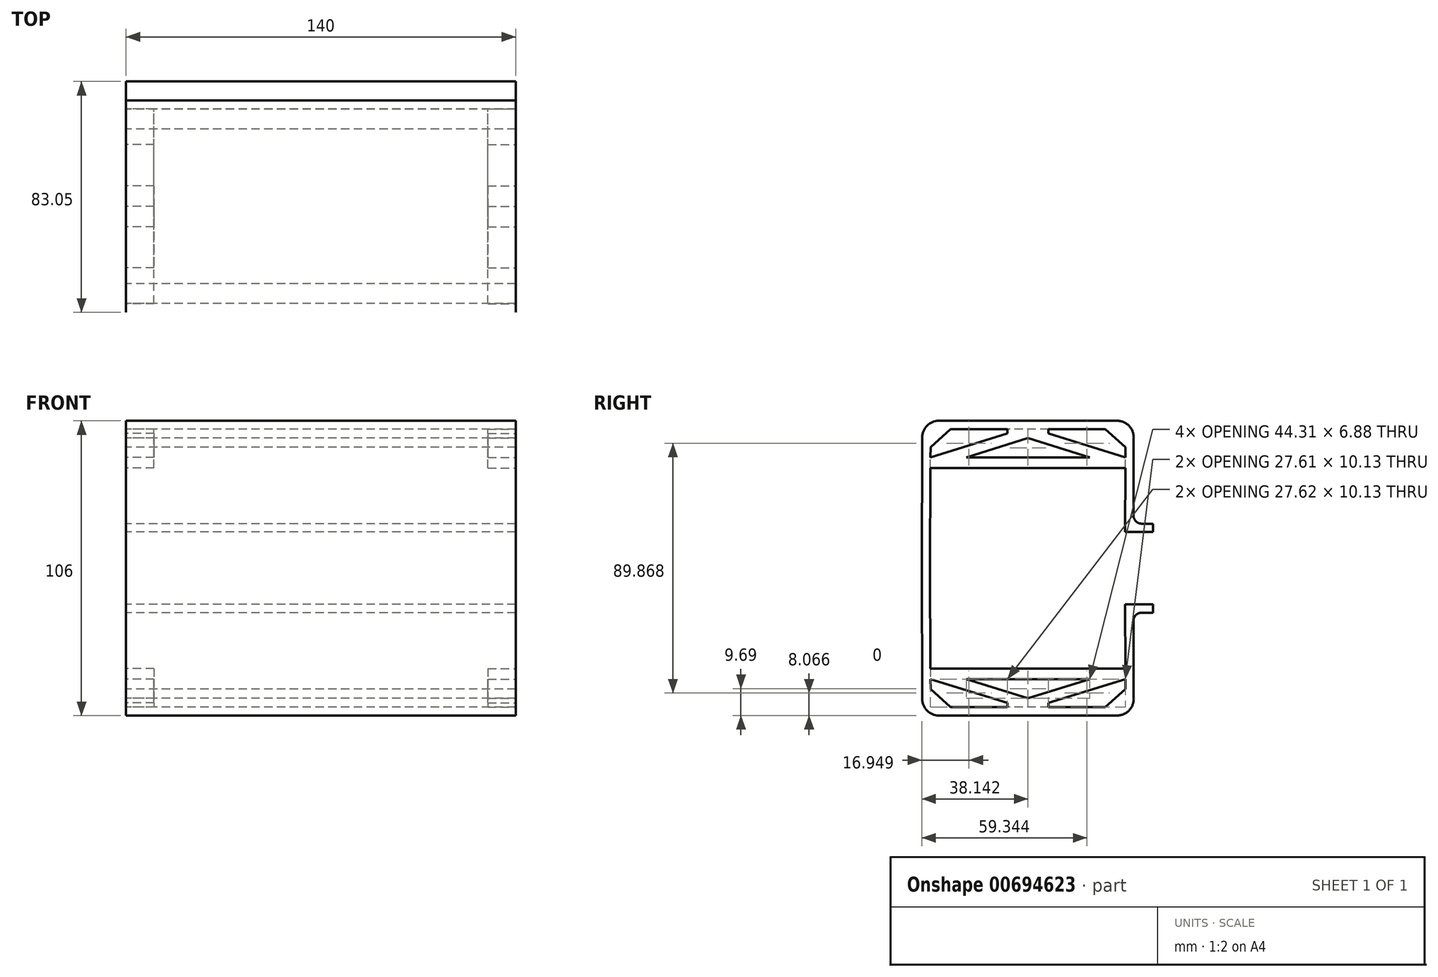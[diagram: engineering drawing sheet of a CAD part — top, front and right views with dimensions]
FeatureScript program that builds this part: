
annotation { "Feature Type Name" : "Feature", "Feature Type Description" : "" }
export const myFeature = defineFeature(function(context is Context, id is Id, definition is map)
    precondition{}
    {
        {
            var Q0;
            Q0=qCreatedBy(makeId("Right.planeOp"),FACE);
            var sketch = newSketch(context, id + "F0", { "sketchPlane" : qUnion([Q0])});
            skLineSegment(sketch, "E0.top", {"start": v(27.8, -50) * mm, "end": v(-27.8, -50) * mm});
            skLineSegment(sketch, "E0.right", {"start": v(-35.15, 0) * mm, "end": v(-35, -43.47) * mm});
            skPoint(sketch, "E0.middle", {"position": v(0, 0) * mm});
            skPoint(sketch, "E1", {"position": v(34.9, -13) * mm});
            skLineSegment(sketch, "E2.trimOffspring", {"start": v(34.9, -13) * mm, "end": v(35, -43.47) * mm});
            skPoint(sketch, "E3.visualSharp", {"position": v(-34.98, -50) * mm});
            skPoint(sketch, "E4.visualSharp", {"position": v(35.02, -50) * mm});
            skLineSegment(sketch, "E5", {"start": v(34.9, -13) * mm, "end": v(44.9, -13) * mm});
            skLineSegment(sketch, "E6.0", {"start": v(40.92, -16) * mm, "end": v(44.9, -16) * mm});
            skLineSegment(sketch, "E6.6", {"start": v(-38.15, 0) * mm, "end": v(-37.99, -47.01) * mm});
            skArc(sketch, "E6.7", {"start": v(-37.99, -47.01) * mm, "mid": v(-36.23, -51.24) * mm, "end": v(-32, -53) * mm});
            skLineSegment(sketch, "E6.8", {"start": v(32, -53) * mm, "end": v(-32, -53) * mm});
            skArc(sketch, "E6.9", {"start": v(32, -53) * mm, "mid": v(36.34, -51.16) * mm, "end": v(38.01, -46.75) * mm});
            skLineSegment(sketch, "E6.10", {"start": v(37.92, -19.01) * mm, "end": v(38.01, -46.75) * mm});
            skLineSegment(sketch, "E7", {"start": v(44.9, -13) * mm, "end": v(44.9, -16) * mm});
            skPoint(sketch, "E8.visualSharp", {"position": v(37.9, -16) * mm});
            skArc(sketch, "E8.filletArc", {"start": v(40.92, -16) * mm, "mid": v(38.8, -16.88) * mm, "end": v(37.92, -19.01) * mm});
            skLineSegment(sketch, "E9", {"start": v(-35.15, 0) * mm, "end": v(-38.15, 0) * mm});
            skLineSegment(sketch, "E10", {"start": v(-38.15, 0) * mm, "end": v(43.63, 0) * mm, "construction": true});
            skLineSegment(sketch, "E11", {"start": v(-35, -43.47) * mm, "end": v(-27.8, -50) * mm});
            skLineSegment(sketch, "E12", {"start": v(35, -43.47) * mm, "end": v(27.8, -50) * mm});
            skSolve(sketch);
        }
        {
            var Q0;
            Q0=qSketchRegion(id+"F0",true);
            extrude(context, id + "F1", {"entities" : qUnion([Q0]), "depth" : 70 * mm, "offsetDistance" : 25 * mm});
        }
        {
            var Q0;
            Q0=makeQuery(id+"F1.opExtrude","CAP_FACE",FACE,{"disambiguationData":[OSD([sQuery(id+"F0.wireOp",EDGE,"E0.bottom"),sQuery(id+"F0.wireOp",EDGE,"E0.top"),sQuery(id+"F0.wireOp",EDGE,"E0.left"),sQuery(id+"F0.wireOp",EDGE,"E0.right"),sQuery(id+"F0.wireOp",EDGE,"E2.trimOffspring"),sQuery(id+"F0.wireOp",EDGE,"16ec7434-7e19-4c96-ad34-d09fe3e63414.filletArc"),sQuery(id+"F0.wireOp",EDGE,"782e88cc-4596-4778-937f-94acf3693ae4.filletArc"),sQuery(id+"F0.wireOp",EDGE,"E3.filletArc"),sQuery(id+"F0.wireOp",EDGE,"E4.filletArc"),sQuery(id+"F0.wireOp",EDGE,"0f476a3a-29cd-4e09-8ddb-883452e4d05f"),sQuery(id+"F0.wireOp",EDGE,"E5"),sQuery(id+"F0.wireOp",EDGE,"E6.0"),sQuery(id+"F0.wireOp",EDGE,"E6.1"),sQuery(id+"F0.wireOp",EDGE,"E6.2"),sQuery(id+"F0.wireOp",EDGE,"E6.3"),sQuery(id+"F0.wireOp",EDGE,"E6.4"),sQuery(id+"F0.wireOp",EDGE,"E6.5"),sQuery(id+"F0.wireOp",EDGE,"E6.6"),sQuery(id+"F0.wireOp",EDGE,"E6.7"),sQuery(id+"F0.wireOp",EDGE,"E6.8"),sQuery(id+"F0.wireOp",EDGE,"E6.9"),sQuery(id+"F0.wireOp",EDGE,"E6.10"),sQuery(id+"F0.wireOp",EDGE,"E7"),sQuery(id+"F0.wireOp",EDGE,"56edb3b3-d3ca-4cde-a283-c5cd5add8c42"),sQuery(id+"F0.wireOp",EDGE,"E8.filletArc"),sQuery(id+"F0.wireOp",EDGE,"69a5be2d-b862-4d8c-9c8a-7a6ed0181d43.filletArc")])],"isStart":false});
            var sketch = newSketch(context, id + "F2", { "sketchPlane" : qUnion([Q0])});
            skLineSegment(sketch, "E13", {"start": v(-35.03, -36.06) * mm, "end": v(34.98, -36.06) * mm});
            skLineSegment(sketch, "E14", {"start": v(-22.17, -39.87) * mm, "end": v(22.15, -39.87) * mm});
            skLineSegment(sketch, "E15", {"start": v(-35.01, -39.87) * mm, "end": v(-7.39, -48.45) * mm});
            skLineSegment(sketch, "E16", {"start": v(-2.39, -50) * mm, "end": v(2.39, -50) * mm});
            skLineSegment(sketch, "E17", {"start": v(7.39, -48.45) * mm, "end": v(34.99, -39.87) * mm});
            skLineSegment(sketch, "E18", {"start": v(0, -46.75) * mm, "end": v(22.15, -39.87) * mm});
            skLineSegment(sketch, "E19", {"start": v(0, -46.75) * mm, "end": v(-22.17, -39.87) * mm});
            skLineSegment(sketch, "E20", {"start": v(-22.17, -39.87) * mm, "end": v(-23.3, -43.5) * mm, "construction": true});
            skLineSegment(sketch, "E21", {"start": v(22.15, -39.87) * mm, "end": v(23.28, -43.5) * mm, "construction": true});
            skLineSegment(sketch, "E22", {"start": v(-0.03, -36.06) * mm, "end": v(0, -39.87) * mm, "construction": true});
            skLineSegment(sketch, "E23", {"start": v(7.39, -48.45) * mm, "end": v(7.39, -50) * mm});
            skLineSegment(sketch, "E24", {"start": v(-7.39, -48.45) * mm, "end": v(-7.39, -50) * mm});
            skSolve(sketch);
        }
        {
            var Q0;
            {var subQ1=sQuery(id+"F2.wireOp",EDGE,"E13");Q0=makeQuery(id+"F2.imprint","IMPRINT",FACE,{"disambiguationData":[TD([[makeQuery(id+"F2.imprint","IMPRINT",EDGE,{"derivedFrom":subQ1}),-1.0]])]});}
            var Q1;
            {var subQ0=sQuery(id+"F2.wireOp",EDGE,"69ec383f-f7ca-4513-a4e7-9af87f1944310.MirrorCS");Q1=makeQuery(id+"F2.imprint","IMPRINT",FACE,{"disambiguationData":[TD([[makeQuery(id+"F2.imprint","IMPRINT",EDGE,{"derivedFrom":subQ0}),-1.0]])]});}
            extrude(context, id + "F3", {"entities" : qUnion([Q0, Q1]), "operationType" : NewBodyOperationType.ADD, "oppositeDirection" : true, "depth" : 10 * mm, "offsetDistance" : 25 * mm});
        }
        {
            var Q0;
            Q0=makeQuery(id+"F1.opExtrude","SWEPT_BODY",BODY,{"disambiguationData":[OSD([sQuery(id+"F0.wireOp",EDGE,"E0.bottom"),sQuery(id+"F0.wireOp",EDGE,"E0.top"),sQuery(id+"F0.wireOp",EDGE,"E0.left"),sQuery(id+"F0.wireOp",EDGE,"E0.right"),sQuery(id+"F0.wireOp",EDGE,"E2.trimOffspring"),sQuery(id+"F0.wireOp",EDGE,"16ec7434-7e19-4c96-ad34-d09fe3e63414.filletArc"),sQuery(id+"F0.wireOp",EDGE,"782e88cc-4596-4778-937f-94acf3693ae4.filletArc"),sQuery(id+"F0.wireOp",EDGE,"E3.filletArc"),sQuery(id+"F0.wireOp",EDGE,"E4.filletArc"),sQuery(id+"F0.wireOp",EDGE,"0f476a3a-29cd-4e09-8ddb-883452e4d05f"),sQuery(id+"F0.wireOp",EDGE,"E5"),sQuery(id+"F0.wireOp",EDGE,"E6.0"),sQuery(id+"F0.wireOp",EDGE,"E6.1"),sQuery(id+"F0.wireOp",EDGE,"E6.2"),sQuery(id+"F0.wireOp",EDGE,"E6.3"),sQuery(id+"F0.wireOp",EDGE,"E6.4"),sQuery(id+"F0.wireOp",EDGE,"E6.5"),sQuery(id+"F0.wireOp",EDGE,"E6.6"),sQuery(id+"F0.wireOp",EDGE,"E6.7"),sQuery(id+"F0.wireOp",EDGE,"E6.8"),sQuery(id+"F0.wireOp",EDGE,"E6.9"),sQuery(id+"F0.wireOp",EDGE,"E6.10"),sQuery(id+"F0.wireOp",EDGE,"E7"),sQuery(id+"F0.wireOp",EDGE,"56edb3b3-d3ca-4cde-a283-c5cd5add8c42"),sQuery(id+"F0.wireOp",EDGE,"E8.filletArc"),sQuery(id+"F0.wireOp",EDGE,"69a5be2d-b862-4d8c-9c8a-7a6ed0181d43.filletArc")])]});
            var Q1;
            Q1=qCreatedBy(makeId("Right.planeOp"),FACE);
            mirror(context, id + "F4", {"operationType" : NewBodyOperationType.ADD, "entities" : qUnion([Q0]), "mirrorPlane" : qUnion([Q1])});
        }
        {
            var Q0;
            Q0=makeQuery(id+"F1.opExtrude","SWEPT_BODY",BODY,{"disambiguationData":[OSD([sQuery(id+"F0.wireOp",EDGE,"E0.top"),sQuery(id+"F0.wireOp",EDGE,"E0.right"),sQuery(id+"F0.wireOp",EDGE,"E2.trimOffspring"),sQuery(id+"F0.wireOp",EDGE,"E3.filletArc"),sQuery(id+"F0.wireOp",EDGE,"E4.filletArc"),sQuery(id+"F0.wireOp",EDGE,"E5"),sQuery(id+"F0.wireOp",EDGE,"E6.0"),sQuery(id+"F0.wireOp",EDGE,"E6.6"),sQuery(id+"F0.wireOp",EDGE,"E6.7"),sQuery(id+"F0.wireOp",EDGE,"E6.8"),sQuery(id+"F0.wireOp",EDGE,"E6.9"),sQuery(id+"F0.wireOp",EDGE,"E6.10"),sQuery(id+"F0.wireOp",EDGE,"E7"),sQuery(id+"F0.wireOp",EDGE,"E8.filletArc"),sQuery(id+"F0.wireOp",EDGE,"E9")])]});
            var Q1;
            Q1=qCreatedBy(makeId("Top.planeOp"),FACE);
            mirror(context, id + "F5", {"operationType" : NewBodyOperationType.ADD, "entities" : qUnion([Q0]), "mirrorPlane" : qUnion([Q1])});
        }
    });
